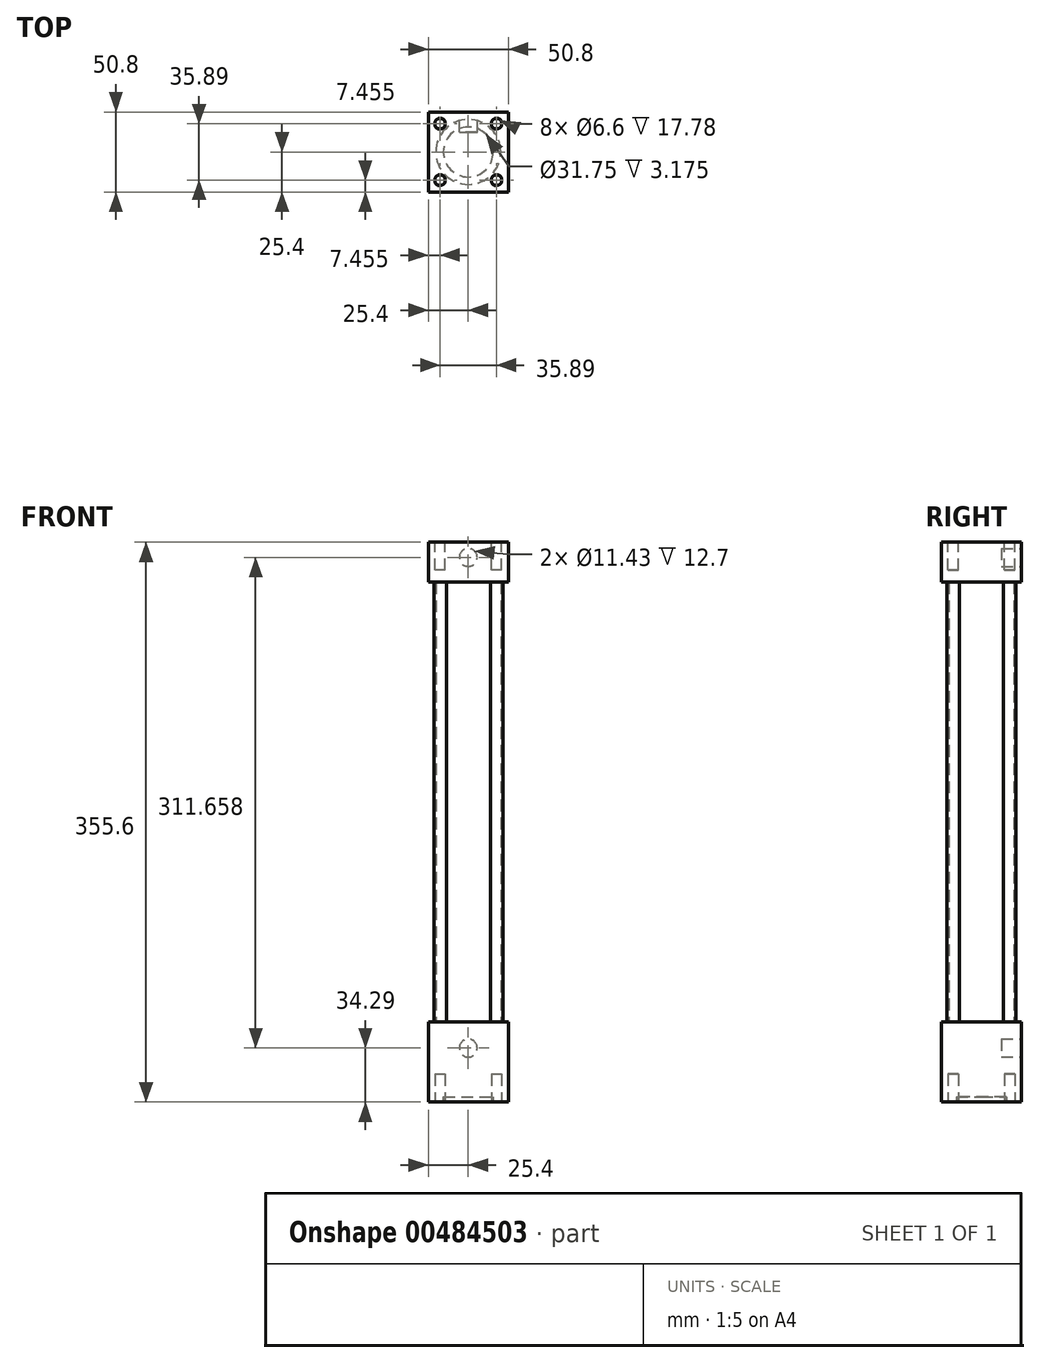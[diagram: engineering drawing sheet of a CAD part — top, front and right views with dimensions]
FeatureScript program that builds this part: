
annotation { "Feature Type Name" : "Feature", "Feature Type Description" : "" }
export const myFeature = defineFeature(function(context is Context, id is Id, definition is map)
    precondition{}
    {
        {
            var Q0;
            Q0=qCreatedBy(makeId("Top.planeOp"),FACE);
            var sketch = newSketch(context, id + "F0", { "sketchPlane" : qUnion([Q0])});
            skCircle(sketch, "E0", {"center": v(0, 0) * mm, "radius": 20.64 * mm});
            skLineSegment(sketch, "E1.bottom", {"start": v(-17.95, 17.95) * mm, "end": v(17.95, 17.95) * mm, "construction": true});
            skLineSegment(sketch, "E1.top", {"start": v(-17.95, -17.95) * mm, "end": v(17.95, -17.95) * mm, "construction": true});
            skLineSegment(sketch, "E1.left", {"start": v(-17.95, 17.95) * mm, "end": v(-17.95, -17.95) * mm, "construction": true});
            skLineSegment(sketch, "E1.right", {"start": v(17.95, 17.95) * mm, "end": v(17.95, -17.95) * mm, "construction": true});
            skCircle(sketch, "E2", {"center": v(-17.95, 17.95) * mm, "radius": 3.96 * mm});
            skCircle(sketch, "E3", {"center": v(17.95, 17.95) * mm, "radius": 3.96 * mm});
            skCircle(sketch, "E4", {"center": v(17.95, -17.95) * mm, "radius": 3.96 * mm});
            skCircle(sketch, "E5", {"center": v(-17.95, -17.95) * mm, "radius": 3.96 * mm});
            skSolve(sketch);
        }
        {
            var Q0;
            Q0 = qSketchRegion(id + "F0", true);
            extrude(context, id + "F1", {"entities" : qUnion([Q0]), "depth" : 279.4 * mm});
        }
        {
            var Q0;
            Q0=makeQuery(id+"F1.opExtrude","CAP_FACE",FACE,{"disambiguationData":[OSD([sQuery(id+"F0.wireOp",EDGE,"E0")])],"isStart":false});
            var sketch = newSketch(context, id + "F2", { "sketchPlane" : qUnion([Q0])});
            skLineSegment(sketch, "E6.bottom", {"start": v(-25.4, 25.4) * mm, "end": v(25.4, 25.4) * mm});
            skLineSegment(sketch, "E6.top", {"start": v(-25.4, -25.4) * mm, "end": v(25.4, -25.4) * mm});
            skLineSegment(sketch, "E6.left", {"start": v(-25.4, 25.4) * mm, "end": v(-25.4, -25.4) * mm});
            skLineSegment(sketch, "E6.right", {"start": v(25.4, 25.4) * mm, "end": v(25.4, -25.4) * mm});
            skPoint(sketch, "E6.middle", {"position": v(0, 0) * mm});
            skSolve(sketch);
        }
        {
            var Q0;
            Q0 = qSketchRegion(id + "F2", true);
            extrude(context, id + "F3", {"entities" : qUnion([Q0]), "operationType" : NewBodyOperationType.ADD, "depth" : 25.4 * mm});
        }
        {
            var Q0;
            Q0=makeQuery(id+"F1.opExtrude","CAP_FACE",FACE,{"disambiguationData":[OSD([sQuery(id+"F0.wireOp",EDGE,"E0")])],"isStart":true});
            var sketch = newSketch(context, id + "F4", { "sketchPlane" : qUnion([Q0])});
            skLineSegment(sketch, "E7.0", {"start": v(-25.4, 25.4) * mm, "end": v(25.4, 25.4) * mm});
            skLineSegment(sketch, "E7.1", {"start": v(-25.4, -25.4) * mm, "end": v(-25.4, 25.4) * mm});
            skLineSegment(sketch, "E7.2", {"start": v(25.4, -25.4) * mm, "end": v(25.4, 25.4) * mm});
            skLineSegment(sketch, "E7.3", {"start": v(-25.4, -25.4) * mm, "end": v(25.4, -25.4) * mm});
            skSolve(sketch);
        }
        {
            var Q0;
            Q0 = qSketchRegion(id + "F4", true);
            extrude(context, id + "F5", {"entities" : qUnion([Q0]), "operationType" : NewBodyOperationType.ADD, "depth" : 50.8 * mm});
        }
        {
            var Q0;
            Q0=makeQuery(id+"F5.opExtrude","CAP_FACE",FACE,{"disambiguationData":[OSD([sQuery(id+"F4.wireOp",EDGE,"E7.0"),sQuery(id+"F4.wireOp",EDGE,"E7.1"),sQuery(id+"F4.wireOp",EDGE,"E7.2"),sQuery(id+"F4.wireOp",EDGE,"E7.3")])],"isStart":false});
            var sketch = newSketch(context, id + "F6", { "sketchPlane" : qUnion([Q0])});
            skCircle(sketch, "E8.0", {"center": v(-17.95, 17.95) * mm, "radius": 3.96 * mm, "construction": true});
            skCircle(sketch, "E8.1", {"center": v(17.95, 17.95) * mm, "radius": 3.96 * mm, "construction": true});
            skCircle(sketch, "E8.2", {"center": v(-17.95, -17.95) * mm, "radius": 3.96 * mm, "construction": true});
            skCircle(sketch, "E8.3", {"center": v(17.95, -17.95) * mm, "radius": 3.96 * mm, "construction": true});
            skCircle(sketch, "E9", {"center": v(-17.95, 17.95) * mm, "radius": 3.3 * mm});
            skCircle(sketch, "E10", {"center": v(17.95, 17.95) * mm, "radius": 3.3 * mm});
            skCircle(sketch, "E11", {"center": v(17.95, -17.95) * mm, "radius": 3.3 * mm});
            skCircle(sketch, "E12", {"center": v(-17.95, -17.95) * mm, "radius": 3.3 * mm});
            skSolve(sketch);
        }
        {
            var Q0;
            Q0 = qSketchRegion(id + "F6", true);
            extrude(context, id + "F7", {"entities" : qUnion([Q0]), "operationType" : NewBodyOperationType.REMOVE, "oppositeDirection" : true, "depth" : 17.78 * mm});
        }
        {
            var Q0;
            Q0=makeQuery(id+"F3.opExtrude","CAP_FACE",FACE,{"disambiguationData":[OSD([sQuery(id+"F2.wireOp",EDGE,"E6.bottom"),sQuery(id+"F2.wireOp",EDGE,"E6.top"),sQuery(id+"F2.wireOp",EDGE,"E6.left"),sQuery(id+"F2.wireOp",EDGE,"E6.right")])],"isStart":false});
            var sketch = newSketch(context, id + "F8", { "sketchPlane" : qUnion([Q0])});
            skCircle(sketch, "E13.0", {"center": v(17.95, -17.95) * mm, "radius": 3.3 * mm});
            skCircle(sketch, "E13.1", {"center": v(-17.95, -17.95) * mm, "radius": 3.3 * mm});
            skCircle(sketch, "E13.2", {"center": v(17.95, 17.95) * mm, "radius": 3.3 * mm});
            skCircle(sketch, "E13.3", {"center": v(-17.95, 17.95) * mm, "radius": 3.3 * mm});
            skSolve(sketch);
        }
        {
            var Q0;
            Q0 = qSketchRegion(id + "F8", true);
            extrude(context, id + "F9", {"entities" : qUnion([Q0]), "operationType" : NewBodyOperationType.REMOVE, "oppositeDirection" : true, "depth" : 17.78 * mm});
        }
        {
            var Q0;
            Q0=makeQuery(id+"F5.opExtrude","CAP_FACE",FACE,{"disambiguationData":[OSD([sQuery(id+"F4.wireOp",EDGE,"E7.0"),sQuery(id+"F4.wireOp",EDGE,"E7.1"),sQuery(id+"F4.wireOp",EDGE,"E7.2"),sQuery(id+"F4.wireOp",EDGE,"E7.3")])],"isStart":false});
            var sketch = newSketch(context, id + "F10", { "sketchPlane" : qUnion([Q0])});
            skCircle(sketch, "E14", {"center": v(0, 0) * mm, "radius": 15.88 * mm});
            skSolve(sketch);
        }
        {
            var Q0;
            Q0 = qSketchRegion(id + "F10", true);
            extrude(context, id + "F11", {"entities" : qUnion([Q0]), "operationType" : NewBodyOperationType.REMOVE, "oppositeDirection" : true, "depth" : 3.17 * mm});
        }
        {
            var Q0;
            Q0=makeQuery(id+"F5.opExtrude","SWEPT_FACE",FACE,{"disambiguationData":[OSD([sQuery(id+"F4.wireOp",EDGE,"E7.3")])]});
            var sketch = newSketch(context, id + "F12", { "sketchPlane" : qUnion([Q0])});
            skCircle(sketch, "E15", {"center": v(0, -16.51) * mm, "radius": 5.72 * mm});
            skCircle(sketch, "E16", {"center": v(0, 295.15) * mm, "radius": 5.72 * mm});
            skSolve(sketch);
        }
        {
            var Q0;
            Q0 = qSketchRegion(id + "F12", true);
            extrude(context, id + "F13", {"entities" : qUnion([Q0]), "operationType" : NewBodyOperationType.REMOVE, "oppositeDirection" : true, "depth" : 12.7 * mm});
        }
    });
